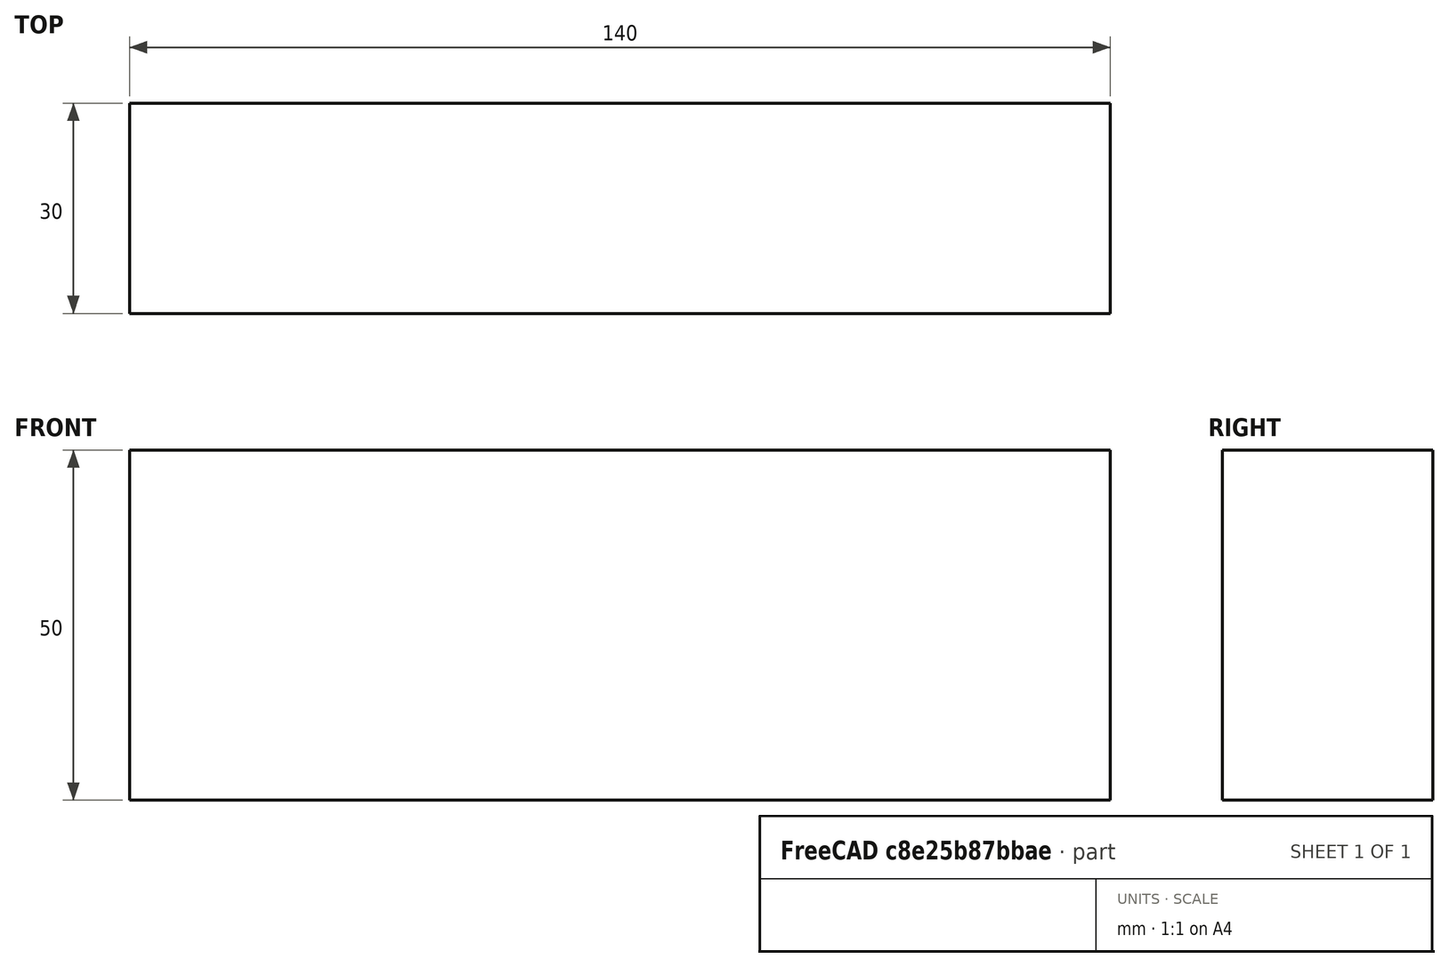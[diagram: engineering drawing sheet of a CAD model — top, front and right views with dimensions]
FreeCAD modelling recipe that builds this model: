
FCSTD DOCUMENT  (FreeCAD 0.15R4671 (Git))
Label: Flat Bar 140x30 EN10058 S235JR
License: All rights reserved
LicenseURL: http://en.wikipedia.org/wiki/All_rights_reserved
objects: Sketcher::SketchObject×1, Part::Extrusion×1
note: 2 computed .brp shape members not serialized (recipe doc carries the construction recipe); baked Part::Feature solids carry a one-line shape summary decoded from their .brp

FEATURE [Sketcher::SketchObject] Sketch
  sketch-geometry (4):
    g0: LineSegment StartX=-70 StartY=-15 StartZ=0 EndX=70 EndY=-15 EndZ=0
    g1: LineSegment StartX=70 StartY=-15 StartZ=0 EndX=70 EndY=15 EndZ=0
    g2: LineSegment StartX=70 StartY=15 StartZ=0 EndX=-70 EndY=15 EndZ=0
    g3: LineSegment StartX=-70 StartY=15 StartZ=0 EndX=-70 EndY=-15 EndZ=0
  constraints (12):
    c: Coincident(g0,g1)
    c: Coincident(g1,g2)
    c: Coincident(g2,g3)
    c: Coincident(g3,g0)
    c: Horizontal(g0)
    c: Horizontal(g2)
    c: Vertical(g1)
    c: Vertical(g3)
    c: Symmetric(g1,g2,g-2)
    c: Symmetric(g0,g1,g-1)
    c: DistanceY(g1) = 30
    c: DistanceX(g0) = 140
FEATURE [Part::Extrusion] Extrude  label="Flat Bar 140x30 EN10058 S235JR"
  Base = -> Sketch
  Dir = (0,0,50)
  Solid = true
